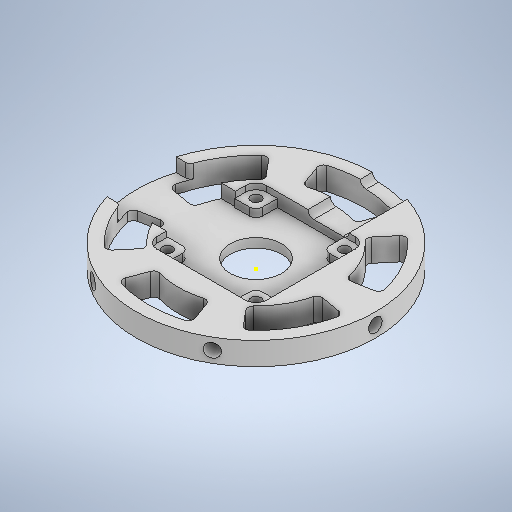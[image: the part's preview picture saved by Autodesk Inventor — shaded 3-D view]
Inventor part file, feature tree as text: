
AUTODESK INVENTOR PART (.ipt)
format: ipt  version: 2025.2 (Build 292293000, 293)  size: 495,104 bytes
history: native  units: mm
features: sketch x9, extrude x7, fillet x4, plane x2, other x1, pattern_circular x1, projected_geometry x1
ambient origin geometry x8: Origin, YZ Plane, XZ Plane, XY Plane, X Axis, Y Axis, Z Axis, Center Point
bodies: Solid1 (feature_tree)
feature tree (25):
  other  "oDrive_micro_housing"
  extrude  "Extrusion1"  Depth=0.1mm
  extrude  "Extrusion2"  Depth=6.7mm
  extrude  "Extrusion3"  Depth=32.3mm
  extrude  "Extrusion4"  Depth=26.0mm
  fillet  "Fillet1"  Radius=26.0mm
  extrude  "Extrusion5"  Depth=20.3mm
  fillet  "Fillet2"  Radius=4.0mm
  sketch  "Sketch6"  dims[d19=3.0mm]
  plane  "Work Plane2"
  extrude  "Extrusion6"  Depth=3.0mm
  pattern_circular  "Circular Pattern1"  [2 undecoded]
  extrude  "Extrusion7"  Depth=1.5mm
  fillet  "Fillet3"  Radius=5.0mm
  fillet  "Fillet4"  Radius=2.3mm
  sketch  "Sketch1"  dims[d0=70.5mm d1=0.1mm]
  sketch  "Sketch2"  dims[d5=0.0mm d6=0.0mm d7=32.3mm]
  sketch  "Sketch3"  dims[d8=32.3mm d9=26.0mm d10=26.0mm]
  sketch  "Sketch4"  dims[d11=3.15mm d14=20.3mm d15=4.0mm d16=0.0mm]
  projected_geometry  "Projected Loop1"
  sketch  "Sketch5"  dims[d17=3.0mm d18=3.0mm]
  plane  "Work Plane1"
  sketch  "Sketch7"  dims[d20=3.0mm]
  sketch  "Sketch8"  dims[d21=2.3mm d22=0.0mm d23=2.0mm d24=12.0mm d25=5.0mm d26=2.3mm d27=0.0mm d28=1.7mm d29=-10.471976mm d30=4.0mm d32=7.0mm d33=0.0mm d34=50.0mm d35=240.0deg d37=1.2mm d38=3.6mm d39=3.490659mm d40=1.745329mm d41=60.0mm d43=360.0deg d45=0.0mm d46=0.0mm d47=1.5mm d48=1.5mm]
  sketch  "Sketch Circular Pattern1"  dims[d2=6.7mm d3=0.0mm d4=15.15mm]
note: 2 required parameter values undecoded (feature->parameter linkage not recoverable at this tier; creation-order binding heuristic only, values carry confidence <= 0.55)
